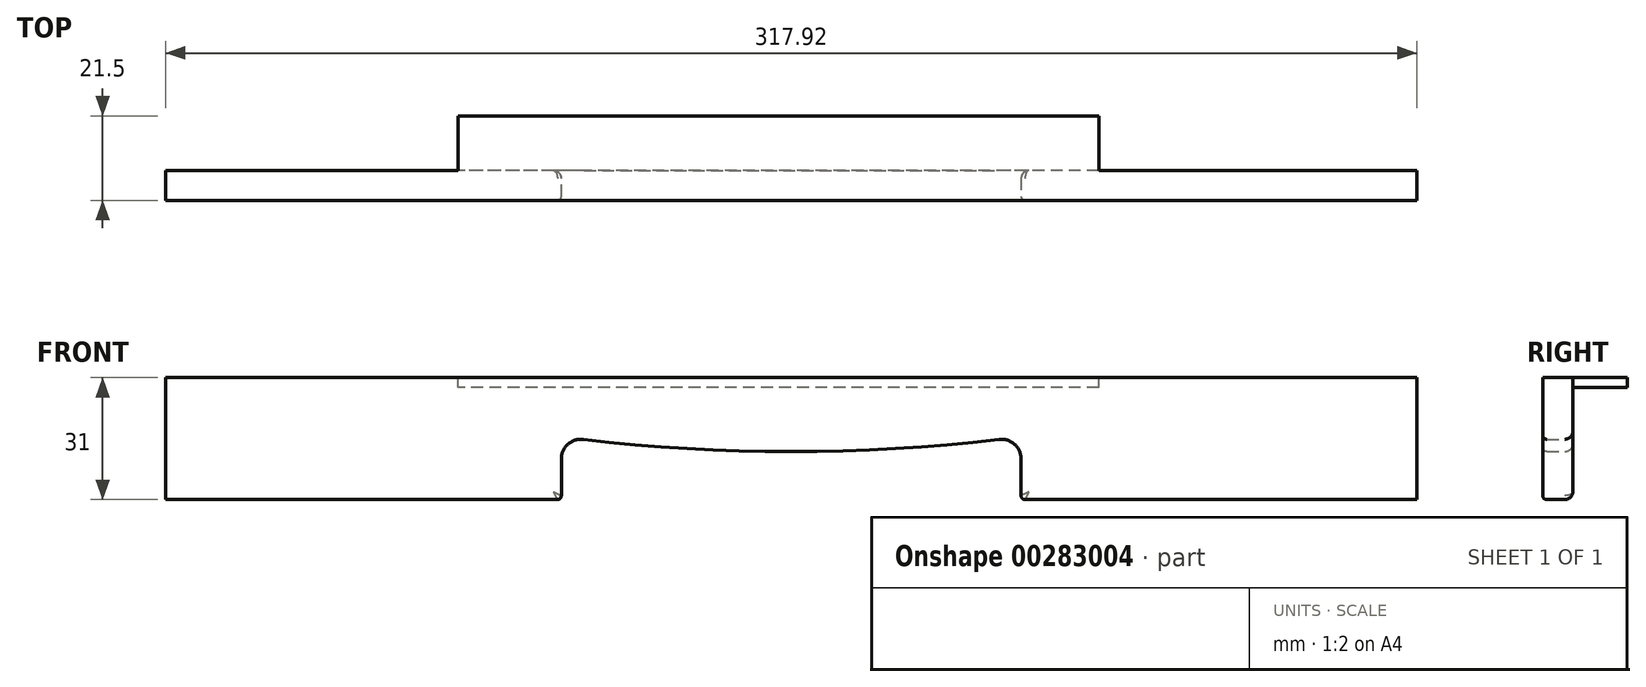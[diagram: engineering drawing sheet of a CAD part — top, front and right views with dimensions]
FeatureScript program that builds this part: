
annotation { "Feature Type Name" : "Feature", "Feature Type Description" : "" }
export const myFeature = defineFeature(function(context is Context, id is Id, definition is map)
    precondition{}
    {
        {
            var Q0;
            Q0=qCreatedBy(makeId("Front.planeOp"),FACE);
            var sketch = newSketch(context, id + "F0", { "sketchPlane" : qUnion([Q0])});
            skArc(sketch, "E0", {"start": v(-58.4, -447.2) * mm, "mid": v(0, -451) * mm, "end": v(58.4, -447.2) * mm});
            skLineSegment(sketch, "E1", {"start": v(-158.96, -432.2) * mm, "end": v(158.96, -432.2) * mm});
            skLineSegment(sketch, "E2", {"start": v(0, 0) * mm, "end": v(0, -650.2) * mm, "construction": true});
            skLineSegment(sketch, "E3", {"start": v(-58.4, -447.2) * mm, "end": v(-58.4, -463.2) * mm});
            skLineSegment(sketch, "E4", {"start": v(58.4, -447.2) * mm, "end": v(58.4, -463.2) * mm});
            skLineSegment(sketch, "E5", {"start": v(158.96, -463.2) * mm, "end": v(58.4, -463.2) * mm});
            skLineSegment(sketch, "E6", {"start": v(-158.96, -463.2) * mm, "end": v(-158.96, -432.2) * mm});
            skLineSegment(sketch, "E7", {"start": v(158.96, -463.2) * mm, "end": v(158.96, -432.2) * mm});
            skLineSegment(sketch, "E8.trimOffspring", {"start": v(-58.4, -463.2) * mm, "end": v(-158.96, -463.2) * mm});
            skSolve(sketch);
        }
        {
            var Q0;
            Q0=qSketchRegion(id+"F0",true);
            extrude(context, id + "F1", {"entities" : qUnion([Q0]), "depth" : 7.6 * mm});
        }
        {
            var Q0;
            Q0=makeQuery(id+"F1.opExtrude","SWEPT_EDGE",EDGE,{"disambiguationData":[OSD([sQuery(id+"F0.wireOp",EDGE,"E0"),sQuery(id+"F0.wireOp",EDGE,"E3")])]});
            var Q1;
            Q1=makeQuery(id+"F1.opExtrude","SWEPT_EDGE",EDGE,{"disambiguationData":[OSD([sQuery(id+"F0.wireOp",EDGE,"E0"),sQuery(id+"F0.wireOp",EDGE,"E4")])]});
            fillet(context, id + "F2", {"entities" : qUnion([Q0, Q1]), "radius" : 5 * mm, "tangentPropagation" : true, "allowEdgeOverflow" : false});
        }
        {
            var Q0;
            Q0=makeQuery(id+"F1.opExtrude","SWEPT_EDGE",EDGE,{"disambiguationData":[OSD([sQuery(id+"F0.wireOp",EDGE,"E4"),sQuery(id+"F0.wireOp",EDGE,"E5")])]});
            var Q1;
            Q1=makeQuery(id+"F1.opExtrude","SWEPT_EDGE",EDGE,{"disambiguationData":[OSD([sQuery(id+"F0.wireOp",EDGE,"E3"),sQuery(id+"F0.wireOp",EDGE,"E8.trimOffspring")])]});
            fillet(context, id + "F3", {"entities" : qUnion([Q0, Q1]), "radius" : 1 * mm, "tangentPropagation" : true, "allowEdgeOverflow" : false});
        }
        {
            var Q0;
            Q0=makeQuery(id+"F1.opExtrude","CAP_EDGE",EDGE,{"disambiguationData":[OSD([sQuery(id+"F0.wireOp",EDGE,"E0")])],"isStart":false});
            fillet(context, id + "F4", {"entities" : qUnion([Q0]), "radius" : 1 * mm, "tangentPropagation" : true, "allowEdgeOverflow" : false});
        }
        {
            var Q0;
            Q0=makeQuery(id+"F1.opExtrude","CAP_EDGE",EDGE,{"disambiguationData":[OSD([sQuery(id+"F0.wireOp",EDGE,"E0")])],"isStart":true});
            fillet(context, id + "F5", {"entities" : qUnion([Q0]), "radius" : 2 * mm, "tangentPropagation" : true, "allowEdgeOverflow" : false});
        }
        {
            var Q0;
            Q0=makeQuery(id+"F1.opExtrude","CAP_FACE",FACE,{"disambiguationData":[OSD([sQuery(id+"F0.wireOp",EDGE,"E0"),sQuery(id+"F0.wireOp",EDGE,"E1"),sQuery(id+"F0.wireOp",EDGE,"E3"),sQuery(id+"F0.wireOp",EDGE,"E4"),sQuery(id+"F0.wireOp",EDGE,"E5"),sQuery(id+"F0.wireOp",EDGE,"E6"),sQuery(id+"F0.wireOp",EDGE,"E7"),sQuery(id+"F0.wireOp",EDGE,"E8.trimOffspring")])],"isStart":true});
            var sketch = newSketch(context, id + "F6", { "sketchPlane" : qUnion([Q0])});
            skLineSegment(sketch, "E9.0", {"start": v(84.68, -432.2) * mm, "end": v(-78.13, -432.2) * mm});
            skLineSegment(sketch, "E10", {"start": v(-78.13, -434.7) * mm, "end": v(84.68, -434.7) * mm});
            skLineSegment(sketch, "E11", {"start": v(84.68, -434.7) * mm, "end": v(84.68, -432.2) * mm});
            skLineSegment(sketch, "E12", {"start": v(-78.13, -434.7) * mm, "end": v(-78.13, -432.2) * mm});
            skPoint(sketch, "E13.orphan", {"position": v(-158.96, -432.2) * mm});
            skPoint(sketch, "E14.orphan", {"position": v(158.96, -432.2) * mm});
            skSolve(sketch);
        }
        {
            var Q0;
            Q0=qSketchRegion(id+"F6",true);
            extrude(context, id + "F7", {"entities" : qUnion([Q0]), "operationType" : NewBodyOperationType.ADD, "depth" : 13.9 * mm});
        }
    });
